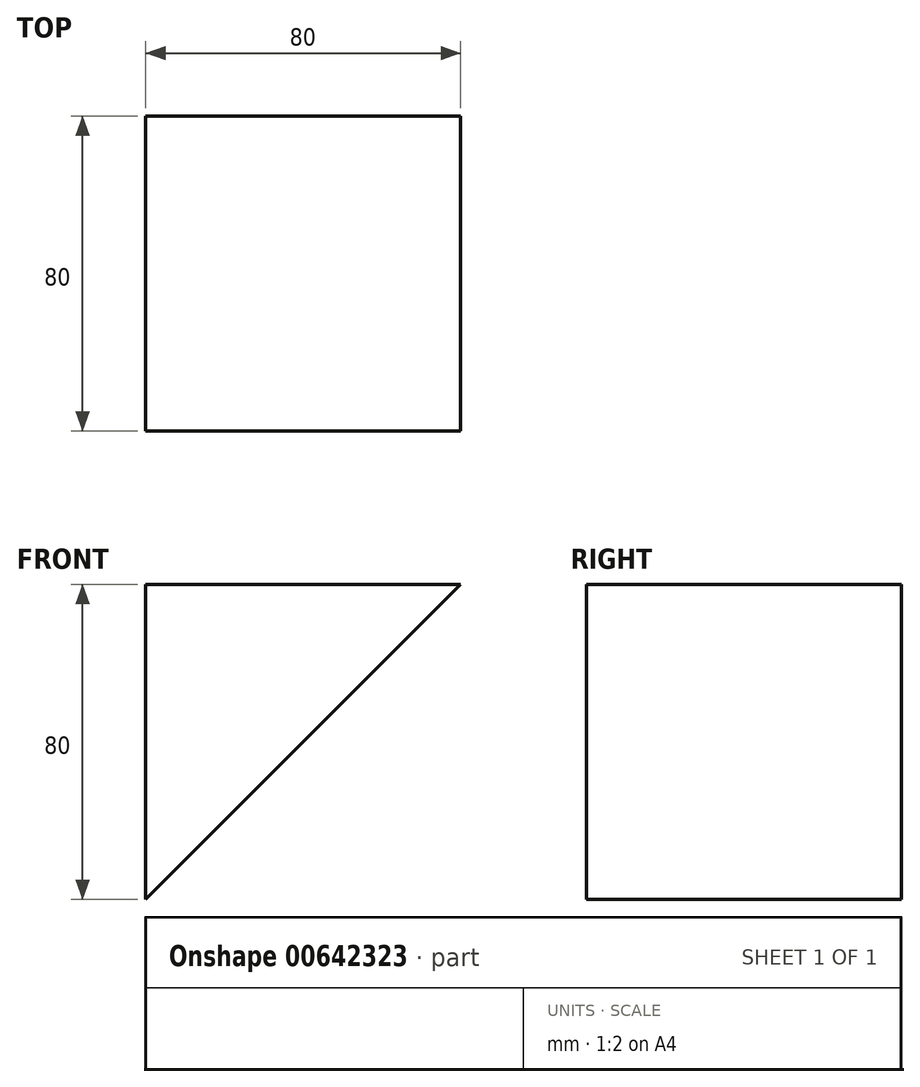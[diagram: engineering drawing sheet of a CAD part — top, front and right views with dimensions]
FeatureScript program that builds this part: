
annotation { "Feature Type Name" : "Feature", "Feature Type Description" : "" }
export const myFeature = defineFeature(function(context is Context, id is Id, definition is map)
    precondition{}
    {
        {
            var Q0;
            Q0=qCreatedBy(makeId("Front.planeOp"),FACE);
            var sketch = newSketch(context, id + "F0", { "sketchPlane" : qUnion([Q0])});
            skLineSegment(sketch, "E0", {"start": v(0, 0) * mm, "end": v(0, 80) * mm});
            skLineSegment(sketch, "E1", {"start": v(0, 80) * mm, "end": v(80, 80) * mm});
            skLineSegment(sketch, "E2", {"start": v(80, 80) * mm, "end": v(0, 0) * mm});
            skSolve(sketch);
        }
        {
            var Q0;
            Q0=makeQuery(id+"F0.imprint","IMPRINT",FACE,{"disambiguationData":[TD([[makeQuery(id+"F0.imprint","IMPRINT",EDGE,{"derivedFrom":sQuery(id+"F0.wireOp",EDGE,"E0")}),-1.0]])]});
            extrude(context, id + "F1", {"entities" : qUnion([Q0]), "depth" : 80 * mm, "offsetDistance" : 25 * mm});
        }
    });
